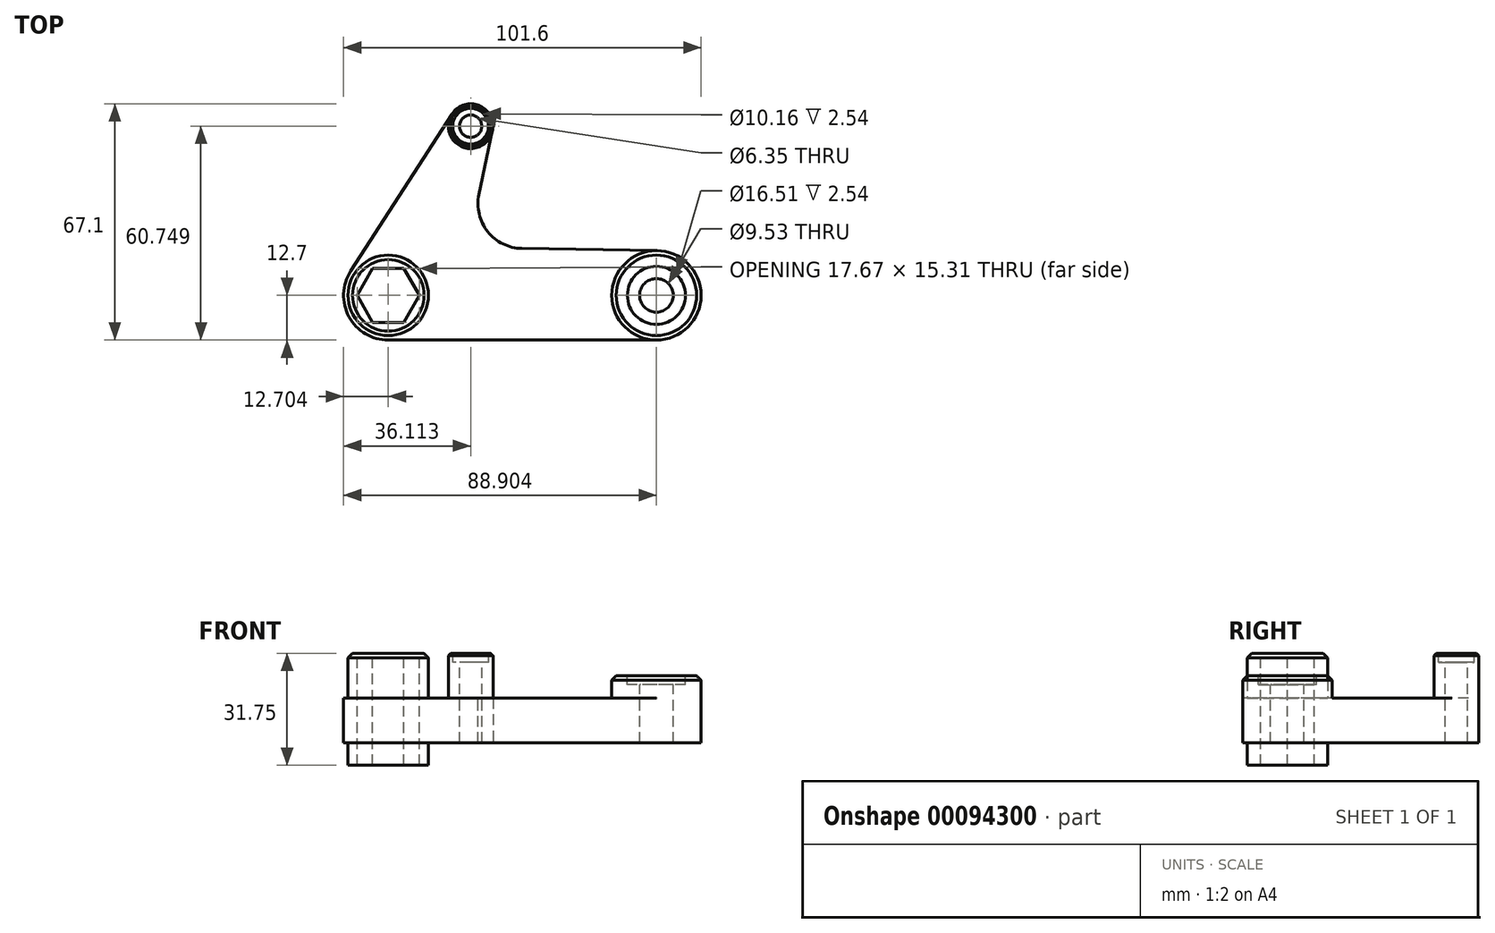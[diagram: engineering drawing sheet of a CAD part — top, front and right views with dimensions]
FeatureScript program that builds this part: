
annotation { "Feature Type Name" : "Feature", "Feature Type Description" : "" }
export const myFeature = defineFeature(function(context is Context, id is Id, definition is map)
    precondition{}
    {
        {
            var Q0;
            Q0=qCreatedBy(makeId("Top.planeOp"),FACE);
            var sketch = newSketch(context, id + "F0", { "sketchPlane" : qUnion([Q0])});
            skArc(sketch, "E0", {"start": v(-50.2, 6.88) * mm, "mid": v(-50.68, -6.08) * mm, "end": v(-39.53, -12.7) * mm});
            skArc(sketch, "E1", {"start": v(36.67, -12.7) * mm, "mid": v(49.37, -0.1) * mm, "end": v(36.88, 12.7) * mm});
            skPoint(sketch, "E2", {"position": v(36.88, 12.7) * mm});
            skPoint(sketch, "E3", {"position": v(36.67, -12.7) * mm});
            skPoint(sketch, "E4", {"position": v(-39.53, -12.7) * mm});
            skLineSegment(sketch, "E5", {"start": v(-39.53, -12.7) * mm, "end": v(36.67, -12.7) * mm});
            skArc(sketch, "E6", {"start": v(-9.9, 46.73) * mm, "mid": v(-13.7, 53.92) * mm, "end": v(-21.46, 51.49) * mm});
            skPoint(sketch, "E7", {"position": v(-21.46, 51.49) * mm});
            skPoint(sketch, "E8", {"position": v(-50.2, 6.88) * mm});
            skLineSegment(sketch, "E9", {"start": v(-21.46, 51.49) * mm, "end": v(-50.2, 6.88) * mm});
            skLineSegment(sketch, "E10", {"start": v(-9.9, 46.73) * mm, "end": v(-16.96, 13.56) * mm});
            skLineSegment(sketch, "E11", {"start": v(-16.96, 13.56) * mm, "end": v(36.88, 12.7) * mm});
            skSolve(sketch);
        }
        {
            var Q0;
            Q0 = qSketchRegion(id + "F0", true);
            extrude(context, id + "F1", {"entities" : qUnion([Q0]), "depth" : 12.7 * mm});
        }
        {
            var Q0;
            Q0 = qSketchRegion(id + "F0", true);
            extrude(context, id + "F2", {"entities" : qUnion([Q0]), "operationType" : NewBodyOperationType.ADD, "depth" : 12.7 * mm});
        }
        {
            var Q0;
            Q0=makeQuery(id+"F1.opExtrude","CAP_FACE",FACE,{"disambiguationData":[OSD([sQuery(id+"F0.wireOp",EDGE,"E0"),sQuery(id+"F0.wireOp",EDGE,"E1"),sQuery(id+"F0.wireOp",EDGE,"E5"),sQuery(id+"F0.wireOp",EDGE,"E6"),sQuery(id+"F0.wireOp",EDGE,"E9"),sQuery(id+"F0.wireOp",EDGE,"E10"),sQuery(id+"F0.wireOp",EDGE,"E11")])],"isStart":false});
            var sketch = newSketch(context, id + "F3", { "sketchPlane" : qUnion([Q0])});
            skCircle(sketch, "E12", {"center": v(-16.12, 48.05) * mm, "radius": 6.35 * mm});
            skSolve(sketch);
        }
        {
            var Q0;
            {var subQ0=sQuery(id+"F3.wireOp",EDGE,"E12");var subQ1=makeQuery(id+"F3.imprint","INTERSECT",VERTEX,{"derivedFrom":[makeQuery(id+"F1.opExtrude","CAP_EDGE",EDGE,{"disambiguationData":[OSD([sQuery(id+"F0.wireOp",EDGE,"E10")])],"isStart":false}),subQ0]});Q0=makeQuery(id+"F3.imprint","IMPRINT",FACE,{"disambiguationData":[TD([[makeQuery(id+"F3.imprint","IMPRINT",EDGE,{"disambiguationData":[TD([[subQ1,-1.0]])],"derivedFrom":subQ0}),1.0]])]});}
            extrude(context, id + "F4", {"entities" : qUnion([Q0]), "operationType" : NewBodyOperationType.ADD, "depth" : 12.7 * mm});
        }
        {
            var Q0;
            Q0=makeQuery(id+"F4.opExtrude","CAP_FACE",FACE,{"disambiguationData":[OSD([sQuery(id+"F3.wireOp",EDGE,"E12")])],"isStart":false});
            var sketch = newSketch(context, id + "F5", { "sketchPlane" : qUnion([Q0])});
            skCircle(sketch, "E13", {"center": v(-16.12, 48.05) * mm, "radius": 5.08 * mm});
            skSolve(sketch);
        }
        {
            var Q0;
            Q0 = qSketchRegion(id + "F5", true);
            extrude(context, id + "F6", {"entities" : qUnion([Q0]), "operationType" : NewBodyOperationType.REMOVE, "oppositeDirection" : true, "depth" : 2.54 * mm});
        }
        {
            var Q0;
            Q0=makeQuery(id+"F4.opExtrude","CAP_EDGE",EDGE,{"disambiguationData":[OSD([sQuery(id+"F3.wireOp",EDGE,"E12")])],"isStart":false});
            chamfer(context, id + "F7", {"entities" : qUnion([Q0]), "width" : 0.64 * mm, "tangentPropagation" : true});
        }
        {
            var Q0;
            Q0=makeQuery(id+"F6.boolean.opBoolean","COPY",FACE,{"derivedFrom":makeQuery(id+"F6.opExtrude","CAP_FACE",FACE,{"disambiguationData":[OSD([sQuery(id+"F5.wireOp",EDGE,"E13")])],"isStart":false})});
            var sketch = newSketch(context, id + "F8", { "sketchPlane" : qUnion([Q0])});
            skCircle(sketch, "E14", {"center": v(-16.12, 48.05) * mm, "radius": 3.17 * mm});
            skSolve(sketch);
        }
        {
            var Q0;
            Q0 = qSketchRegion(id + "F8", true);
            extrude(context, id + "F9", {"entities" : qUnion([Q0]), "operationType" : NewBodyOperationType.REMOVE, "endBound" : BoundingType.THROUGH_ALL, "oppositeDirection" : true, "depth" : 25.4 * mm});
        }
        {
            var Q0;
            Q0=makeQuery(id+"F1.opExtrude","SWEPT_EDGE",EDGE,{"disambiguationData":[OSD([sQuery(id+"F0.wireOp",EDGE,"E10"),sQuery(id+"F0.wireOp",EDGE,"E11")])]});
            fillet(context, id + "F10", {"entities" : qUnion([Q0]), "radius" : 12.7 * mm, "tangentPropagation" : true, "allowEdgeOverflow" : false});
        }
        {
            var Q0;
            Q0=makeQuery(id+"F1.opExtrude","CAP_FACE",FACE,{"disambiguationData":[OSD([sQuery(id+"F0.wireOp",EDGE,"E0"),sQuery(id+"F0.wireOp",EDGE,"E1"),sQuery(id+"F0.wireOp",EDGE,"E5"),sQuery(id+"F0.wireOp",EDGE,"E6"),sQuery(id+"F0.wireOp",EDGE,"E9"),sQuery(id+"F0.wireOp",EDGE,"E10"),sQuery(id+"F0.wireOp",EDGE,"E11")])],"isStart":false});
            var sketch = newSketch(context, id + "F11", { "sketchPlane" : qUnion([Q0])});
            skCircle(sketch, "E15", {"center": v(36.67, 0) * mm, "radius": 12.7 * mm});
            skSolve(sketch);
        }
        {
            var Q0;
            Q0 = qSketchRegion(id + "F11", true);
            extrude(context, id + "F12", {"entities" : qUnion([Q0]), "operationType" : NewBodyOperationType.ADD, "depth" : 6.35 * mm});
        }
        {
            var Q0;
            Q0=makeQuery(id+"F12.opExtrude","CAP_FACE",FACE,{"disambiguationData":[OSD([sQuery(id+"F11.wireOp",EDGE,"E15")])],"isStart":false});
            var sketch = newSketch(context, id + "F13", { "sketchPlane" : qUnion([Q0])});
            skCircle(sketch, "E16", {"center": v(36.67, 0) * mm, "radius": 8.26 * mm});
            skSolve(sketch);
        }
        {
            var Q0;
            Q0 = qSketchRegion(id + "F13", true);
            extrude(context, id + "F14", {"entities" : qUnion([Q0]), "operationType" : NewBodyOperationType.REMOVE, "oppositeDirection" : true, "depth" : 2.54 * mm});
        }
        {
            var Q0;
            Q0=makeQuery(id+"F14.boolean.opBoolean","COPY",FACE,{"derivedFrom":makeQuery(id+"F14.opExtrude","CAP_FACE",FACE,{"disambiguationData":[OSD([sQuery(id+"F13.wireOp",EDGE,"E16")])],"isStart":false})});
            var sketch = newSketch(context, id + "F15", { "sketchPlane" : qUnion([Q0])});
            skCircle(sketch, "E17", {"center": v(36.67, 0) * mm, "radius": 4.76 * mm});
            skSolve(sketch);
        }
        {
            var Q0;
            Q0 = qSketchRegion(id + "F15", true);
            extrude(context, id + "F16", {"entities" : qUnion([Q0]), "operationType" : NewBodyOperationType.REMOVE, "endBound" : BoundingType.THROUGH_ALL, "oppositeDirection" : true, "depth" : 25.4 * mm});
        }
        {
            var Q0;
            Q0=makeQuery(id+"F1.opExtrude","CAP_FACE",FACE,{"disambiguationData":[OSD([sQuery(id+"F0.wireOp",EDGE,"E0"),sQuery(id+"F0.wireOp",EDGE,"E1"),sQuery(id+"F0.wireOp",EDGE,"E5"),sQuery(id+"F0.wireOp",EDGE,"E6"),sQuery(id+"F0.wireOp",EDGE,"E9"),sQuery(id+"F0.wireOp",EDGE,"E10"),sQuery(id+"F0.wireOp",EDGE,"E11")])],"isStart":false});
            var sketch = newSketch(context, id + "F17", { "sketchPlane" : qUnion([Q0])});
            skCircle(sketch, "E18", {"center": v(-39.53, 0) * mm, "radius": 11.43 * mm});
            skSolve(sketch);
        }
        {
            var Q0;
            Q0=makeQuery(id+"F17.imprint","IMPRINT",FACE,{"disambiguationData":[TD([[makeQuery(id+"F17.imprint","IMPRINT",EDGE,{"derivedFrom":sQuery(id+"F17.wireOp",EDGE,"E18")}),1.0]])]});
            extrude(context, id + "F18", {"entities" : qUnion([Q0]), "operationType" : NewBodyOperationType.ADD, "depth" : 12.7 * mm, "hasSecondDirection" : true, "secondDirectionOppositeDirection" : true, "secondDirectionDepth" : 19.05 * mm});
        }
        {
            var Q0;
            Q0=makeQuery(id+"F18.opExtrude","CAP_FACE",FACE,{"disambiguationData":[OSD([sQuery(id+"F17.wireOp",EDGE,"E18")])],"isStart":false});
            var sketch = newSketch(context, id + "F19", { "sketchPlane" : qUnion([Q0])});
            skCircle(sketch, "E19.cCircle", {"center": v(-39.53, 0) * mm, "radius": 7.65 * mm, "construction": true});
            skLineSegment(sketch, "E19.0", {"start": v(-43.94, 7.65) * mm, "end": v(-35.1, 7.65) * mm});
            skLineSegment(sketch, "E19.1", {"start": v(-35.1, 7.65) * mm, "end": v(-30.69, 0) * mm});
            skLineSegment(sketch, "E19.2", {"start": v(-30.69, 0) * mm, "end": v(-35.1, -7.65) * mm});
            skLineSegment(sketch, "E19.3", {"start": v(-35.1, -7.65) * mm, "end": v(-43.94, -7.65) * mm});
            skLineSegment(sketch, "E19.4", {"start": v(-43.94, -7.65) * mm, "end": v(-48.36, 0) * mm});
            skLineSegment(sketch, "E19.5", {"start": v(-48.36, 0) * mm, "end": v(-43.94, 7.65) * mm});
            skPoint(sketch, "E19.0.midPoint", {"position": v(-39.53, 7.65) * mm});
            skSolve(sketch);
        }
        {
            var Q0;
            Q0 = qSketchRegion(id + "F19", true);
            extrude(context, id + "F20", {"entities" : qUnion([Q0]), "operationType" : NewBodyOperationType.REMOVE, "endBound" : BoundingType.THROUGH_ALL, "oppositeDirection" : true, "depth" : 25.4 * mm});
        }
        {
            var Q0;
            Q0=makeQuery(id+"F18.opExtrude","CAP_EDGE",EDGE,{"disambiguationData":[OSD([sQuery(id+"F17.wireOp",EDGE,"E18")])],"isStart":false});
            var Q1;
            Q1=makeQuery(id+"F12.opExtrude","CAP_EDGE",EDGE,{"disambiguationData":[OSD([sQuery(id+"F11.wireOp",EDGE,"E15")])],"isStart":false});
            chamfer(context, id + "F21", {"entities" : qUnion([Q0, Q1]), "width" : 1.27 * mm, "tangentPropagation" : true});
        }
    });
